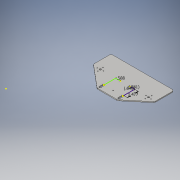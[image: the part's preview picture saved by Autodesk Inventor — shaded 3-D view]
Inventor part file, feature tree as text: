
AUTODESK INVENTOR PART (.ipt)
format: ipt  version: 2016 (Build 200138000, 138)  size: 233,472 bytes
history: native  units: in
note: dims shown in document units (in); Inventor stores cm internally (conversion verified against a paired STEP export)
features: sketch x8, extrude x4, hole x3
ambient origin geometry x8: Origin, YZ Plane, XZ Plane, XY Plane, X Axis, Y Axis, Z Axis, Center Point
bodies: Solid1 (feature_tree)
feature tree (15):
  extrude  "Extrusion1"  Depth=8.5in
  hole  "Hole1"  [1 undecoded]
  extrude  "Extrusion3"  Depth=3.1102in
  extrude  "Extrusion4"  Depth=0.25in
  extrude  "Extrusion5"  Depth=1.0236in
  hole  "Hole2"  [1 undecoded]
  hole  "Hole4"  [1 undecoded]
  sketch  "Sketch13"  dims[d43=1.0in d44=0.0in d45=1.75in d47=1.75in d48=1.75in d49=1.75in d50=2.382in d52=2.5591in d53=0.6398in d54=0.6398in d55=2.382in d58=2.0472in d62=1.2795in d64=0.1181in d65=0.75in d66=0.375in d67=0.25in d68=0.5635in d69=1.0in d70=0.8108in d72=0.25in d76=0.236in d77=0.492in d78=0.236in d79=0.492in d80=1.0in d81=0.0in d82=0.236in d83=0.492in d84=0.236in d85=0.492in d86=1.0in d87=0.0in d88=0.25in d93=0.2953in d96=2.07in d100=0.25in d101=0.25in d102=0.25in d103=0.25in d104=0.962in d125=0.0in d159=1.5748in d161=360.0deg d167=0.107in d168=0.75in d169=0.375in d170=0.25in d171=0.5635in d172=1.0in d173=0.8108in d174=0.7664in d175=0.7664in d176=1.5748in d178=360.0deg d180=2.5591in d181=1.2795in d182=1.4767in d183=0.5808in d184=0.6399in d185=0.5876in d186=2.5165in]
  sketch  "Sketch1"  dims[d0=8.5in d1=6.0in]
  sketch  "Sketch2"  dims[d2=0.125in d3=0.0in d4=5.6831in]
  sketch  "Sketch3"  dims[d5=1.0236in d7=3.1102in]
  sketch  "Sketch5"  dims[d12=0.25in d13=0.75in d14=0.375in d15=0.25in d16=0.5635in d17=1.0in d18=0.8108in d19=1.0768in]
  sketch  "Sketch7"  dims[d20=3.1102in d21=1.0236in]
  sketch  "Sketch8"  dims[d22=3.124in d23=7.5728in]
  sketch  "Sketch11"  dims[d24=0.2953in d40=3.8881in]
note: 3 required parameter values undecoded (feature->parameter linkage not recoverable at this tier; creation-order binding heuristic only, values carry confidence <= 0.55)
